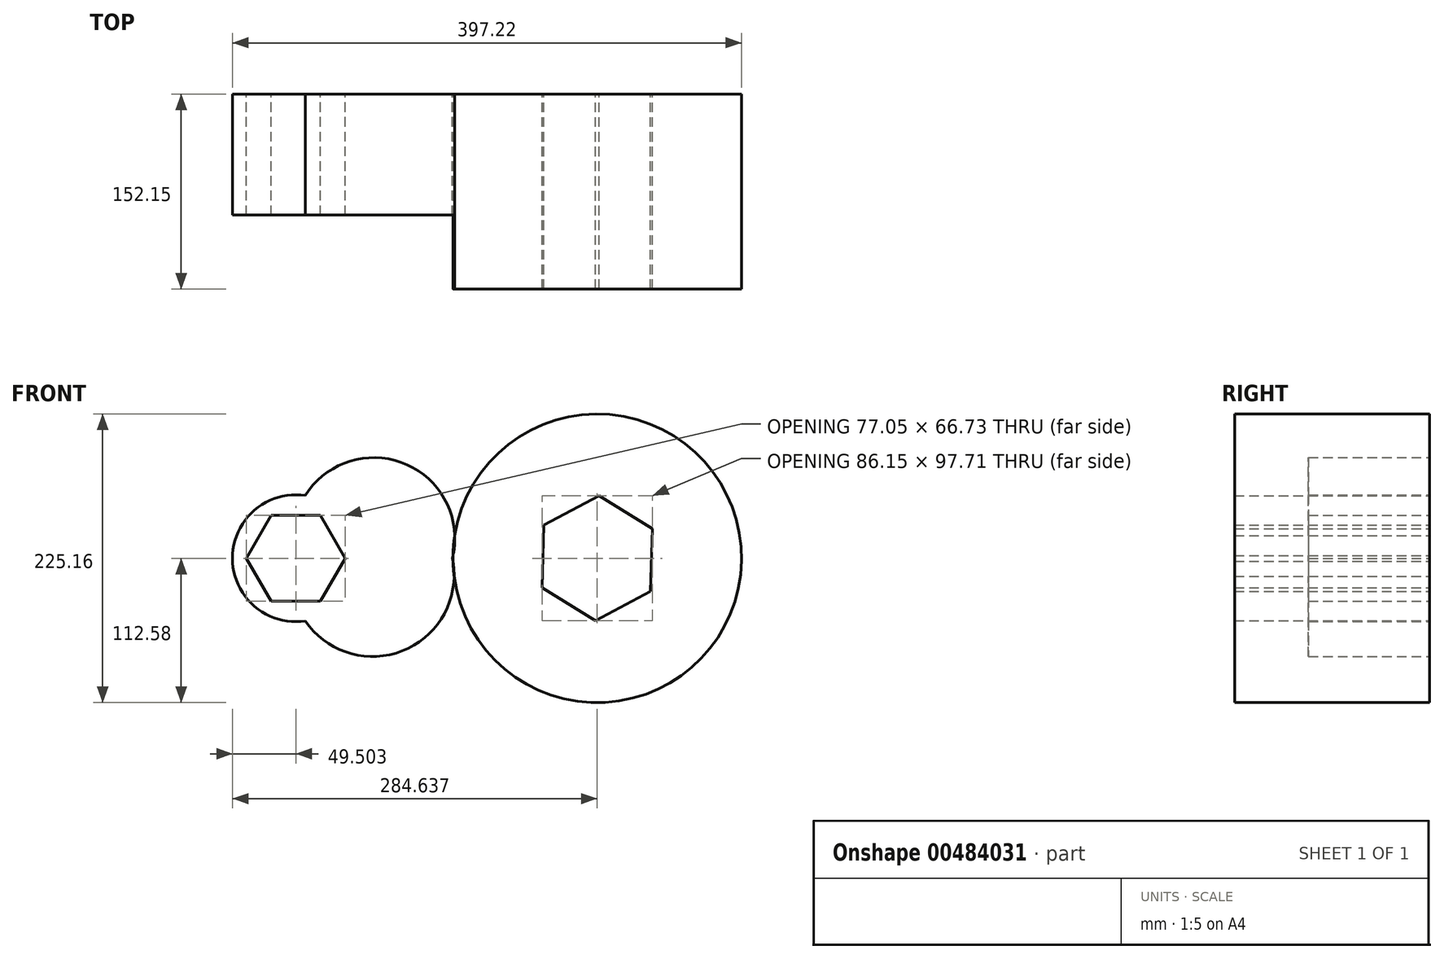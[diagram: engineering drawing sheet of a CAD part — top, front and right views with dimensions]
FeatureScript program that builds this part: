
annotation { "Feature Type Name" : "Feature", "Feature Type Description" : "" }
export const myFeature = defineFeature(function(context is Context, id is Id, definition is map)
    precondition{}
    {
        {
            var Q0;
            Q0=qCreatedBy(makeId("Front.planeOp"),FACE);
            var sketch = newSketch(context, id + "F0", { "sketchPlane" : qUnion([Q0])});
            skLineSegment(sketch, "E0", {"start": v(0, 0) * mm, "end": v(-122.12, 0) * mm});
            skLineSegment(sketch, "E1", {"start": v(-122.12, 0) * mm, "end": v(113.02, 0) * mm});
            skCircle(sketch, "E2", {"center": v(-122.12, 0) * mm, "radius": 49.5 * mm});
            skCircle(sketch, "E3", {"center": v(113.02, 0) * mm, "radius": 112.58 * mm});
            skArc(sketch, "E4", {"start": v(0, 0) * mm, "mid": v(-36.49, 73.47) * mm, "end": v(-114.77, 48.96) * mm});
            skArc(sketch, "E5", {"start": v(-114.77, -48.96) * mm, "mid": v(-37.31, -71.54) * mm, "end": v(0, 0) * mm});
            skCircle(sketch, "E6.cCircle", {"center": v(113.02, 0) * mm, "radius": 42.33 * mm, "construction": true});
            skLineSegment(sketch, "E6.0", {"start": v(111.49, -48.86) * mm, "end": v(69.94, -23.1) * mm});
            skLineSegment(sketch, "E6.1", {"start": v(69.94, -23.1) * mm, "end": v(71.47, 25.75) * mm});
            skLineSegment(sketch, "E6.2", {"start": v(71.47, 25.75) * mm, "end": v(114.55, 48.86) * mm});
            skLineSegment(sketch, "E6.3", {"start": v(114.55, 48.86) * mm, "end": v(156.1, 23.1) * mm});
            skLineSegment(sketch, "E6.4", {"start": v(156.1, 23.1) * mm, "end": v(154.56, -25.75) * mm});
            skLineSegment(sketch, "E6.5", {"start": v(154.56, -25.75) * mm, "end": v(111.49, -48.86) * mm});
            skPoint(sketch, "E6.0.midPoint", {"position": v(90.71, -35.98) * mm});
            skCircle(sketch, "E7", {"center": v(113.02, 0) * mm, "radius": 42.33 * mm});
            skCircle(sketch, "E8.cCircle", {"center": v(-122.12, 0) * mm, "radius": 33.36 * mm, "construction": true});
            skLineSegment(sketch, "E8.0", {"start": v(-102.85, -33.36) * mm, "end": v(-141.38, -33.36) * mm});
            skLineSegment(sketch, "E8.1", {"start": v(-141.38, -33.36) * mm, "end": v(-160.64, 0) * mm});
            skLineSegment(sketch, "E8.2", {"start": v(-160.64, 0) * mm, "end": v(-141.38, 33.36) * mm});
            skLineSegment(sketch, "E8.3", {"start": v(-141.38, 33.36) * mm, "end": v(-102.85, 33.36) * mm});
            skLineSegment(sketch, "E8.4", {"start": v(-102.85, 33.36) * mm, "end": v(-83.6, 0) * mm});
            skLineSegment(sketch, "E8.5", {"start": v(-83.6, 0) * mm, "end": v(-102.85, -33.36) * mm});
            skPoint(sketch, "E8.0.midPoint", {"position": v(-122.12, -33.36) * mm});
            skSolve(sketch);
        }
        {
            var Q0;
            {var subQ1=sQuery(id+"F0.wireOp",EDGE,"E1");var subQ10=sQuery(id+"F0.wireOp",EDGE,"E3");var subQ14=makeQuery(id+"F0.imprint","INTERSECT",VERTEX,{"derivedFrom":[subQ1,subQ10]});Q0=makeQuery(id+"F0.imprint","IMPRINT",FACE,{"disambiguationData":[TD([[makeQuery(id+"F0.imprint","IMPRINT",EDGE,{"disambiguationData":[TD([[subQ14,1.0]])],"derivedFrom":subQ10}),1.0]])]});}
            extrude(context, id + "F1", {"entities" : qUnion([Q0]), "depth" : 152.15 * mm});
        }
        {
            var Q0;
            Q0=makeQuery(id+"F0.imprint","IMPRINT",FACE,{"disambiguationData":[TD([[makeQuery(id+"F0.imprint","IMPRINT",EDGE,{"derivedFrom":sQuery(id+"F0.wireOp",EDGE,"E8.0")}),1.0]])]});
            var Q1;
            {var subQ0=sQuery(id+"F0.wireOp",EDGE,"E4");var subQ5=sQuery(id+"F0.wireOp",EDGE,"E2");var subQ8=makeQuery(id+"F0.imprint","INTERSECT",VERTEX,{"derivedFrom":[subQ5,subQ0]});Q1=makeQuery(id+"F0.imprint","IMPRINT",FACE,{"disambiguationData":[TD([[makeQuery(id+"F0.imprint","IMPRINT",EDGE,{"disambiguationData":[TD([[subQ8,1.0]])],"derivedFrom":subQ5}),-1.0]])]});}
            var Q2;
            {var subQ0=sQuery(id+"F0.wireOp",EDGE,"E5");var subQ1=sQuery(id+"F0.wireOp",EDGE,"E2");var subQ2=makeQuery(id+"F0.imprint","INTERSECT",VERTEX,{"derivedFrom":[subQ1,subQ0]});Q2=makeQuery(id+"F0.imprint","IMPRINT",FACE,{"disambiguationData":[TD([[makeQuery(id+"F0.imprint","IMPRINT",EDGE,{"disambiguationData":[TD([[subQ2,-1.0]])],"derivedFrom":subQ1}),-1.0]])]});}
            extrude(context, id + "F2", {"entities" : qUnion([Q0, Q1, Q2]), "depth" : 94.49 * mm});
        }
    });
